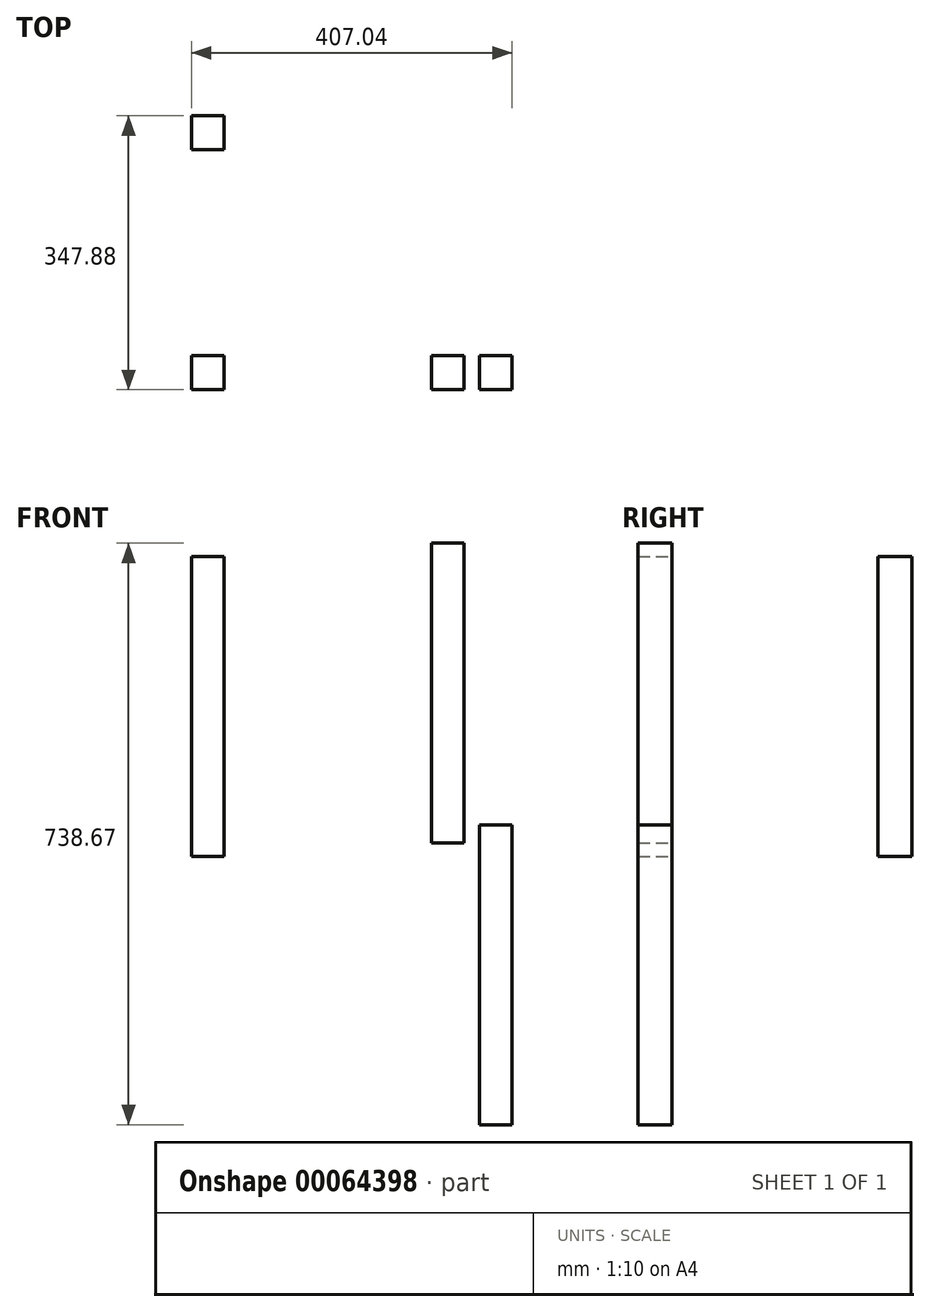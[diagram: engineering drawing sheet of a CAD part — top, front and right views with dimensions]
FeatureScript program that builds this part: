
annotation { "Feature Type Name" : "Feature", "Feature Type Description" : "" }
export const myFeature = defineFeature(function(context is Context, id is Id, definition is map)
    precondition{}
    {
        {
            var Q0;
            Q0=qCreatedBy(makeId("Top.planeOp"),FACE);
            var sketch = newSketch(context, id + "F0", { "sketchPlane" : qUnion([Q0])});
            skLineSegment(sketch, "E0.rect.bottom", {"start": v(-310.33, 244.26) * mm, "end": v(-351.75, 244.26) * mm});
            skLineSegment(sketch, "E0.rect.top", {"start": v(-310.33, 287.34) * mm, "end": v(-351.75, 287.34) * mm});
            skLineSegment(sketch, "E0.rect.left", {"start": v(-310.33, 244.26) * mm, "end": v(-310.33, 287.34) * mm});
            skLineSegment(sketch, "E0.rect.right", {"start": v(-351.75, 244.26) * mm, "end": v(-351.75, 287.34) * mm});
            skPoint(sketch, "E0.rect.middle", {"position": v(-331.04, 265.8) * mm});
            skSolve(sketch);
        }
        {
            var Q0;
            Q0 = qSketchRegion(id + "F0", true);
            extrude(context, id + "F1", {"entities" : qUnion([Q0]), "depth" : 355.6 * mm, "hasSecondDirection" : true, "secondDirectionOppositeDirection" : true, "secondDirectionDepth" : 25.4 * mm});
        }
        {
            var Q0;
            Q0=makeQuery(id+"F1.opExtrude","SWEPT_BODY",BODY,{"disambiguationData":[OSD([sQuery(id+"F0.wireOp",EDGE,"E0.rect.bottom"),sQuery(id+"F0.wireOp",EDGE,"E0.rect.top"),sQuery(id+"F0.wireOp",EDGE,"E0.rect.left"),sQuery(id+"F0.wireOp",EDGE,"E0.rect.right")])]});
            transform(context, id + "F2", {"entities" : qUnion([Q0]), "transformType" : TransformType.TRANSLATION_3D, "dx" : 0 * mm, "dy" : 304.8 * mm, "dz" : 0 * mm, "makeCopy" : true});
        }
        {
            var Q0;
            Q0=makeQuery(id+"F1.opExtrude","SWEPT_BODY",BODY,{"disambiguationData":[OSD([sQuery(id+"F0.wireOp",EDGE,"E0.rect.bottom"),sQuery(id+"F0.wireOp",EDGE,"E0.rect.top"),sQuery(id+"F0.wireOp",EDGE,"E0.rect.left"),sQuery(id+"F0.wireOp",EDGE,"E0.rect.right")])]});
            transform(context, id + "F3", {"entities" : qUnion([Q0]), "transformType" : TransformType.TRANSLATION_3D, "dx" : 304.8 * mm, "dy" : 0 * mm, "dz" : 16.62 * mm, "makeCopy" : true});
        }
        {
            var Q0;
            Q0=makeQuery(id+"F1.opExtrude","SWEPT_BODY",BODY,{"disambiguationData":[OSD([sQuery(id+"F0.wireOp",EDGE,"E0.rect.bottom"),sQuery(id+"F0.wireOp",EDGE,"E0.rect.top"),sQuery(id+"F0.wireOp",EDGE,"E0.rect.left"),sQuery(id+"F0.wireOp",EDGE,"E0.rect.right")])]});
            transform(context, id + "F4", {"entities" : qUnion([Q0]), "transformType" : TransformType.TRANSLATION_3D, "dx" : 365.62 * mm, "dy" : 0 * mm, "dz" : -341.05 * mm, "makeCopy" : true});
        }
    });
